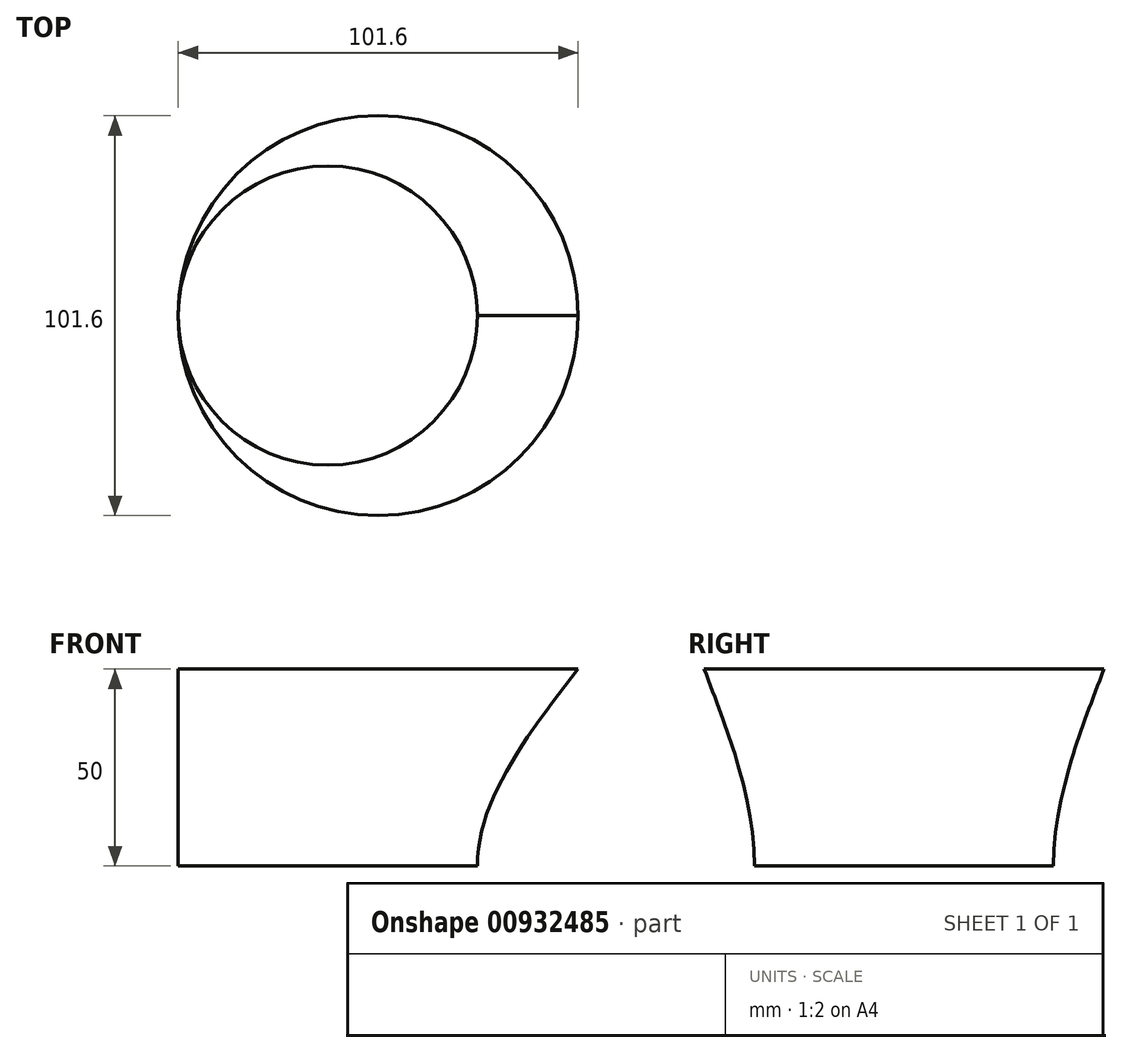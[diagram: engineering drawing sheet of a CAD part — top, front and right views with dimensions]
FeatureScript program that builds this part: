
annotation { "Feature Type Name" : "Feature", "Feature Type Description" : "" }
export const myFeature = defineFeature(function(context is Context, id is Id, definition is map)
    precondition{}
    {
        {
            var Q0;
            Q0=qCreatedBy(makeId("Top.planeOp"),FACE);
            var sketch = newSketch(context, id + "F0", { "sketchPlane" : qUnion([Q0])});
            skCircle(sketch, "E0", {"center": v(0, 0) * mm, "radius": 50.8 * mm});
            skSolve(sketch);
        }
        {
            var Q0;
            Q0=qCreatedBy(makeId("Top.planeOp"),FACE);
            cPlane(context, id + "F1", {"entities" : qUnion([Q0]), "cplaneType" : CPlaneType.OFFSET, "offset" : 50 * mm, "oppositeDirection" : true, "width" : 150 * mm, "height" : 150 * mm});
        }
        {
            var Q0;
            Q0=qCreatedBy(id+"F1.planeOp",FACE);
            var sketch = newSketch(context, id + "F2", { "sketchPlane" : qUnion([Q0])});
            skCircle(sketch, "E1.0", {"center": v(0, 0) * mm, "radius": 50.8 * mm});
            skCircle(sketch, "E2", {"center": v(-12.8, 0) * mm, "radius": 38 * mm});
            skPoint(sketch, "E2.first.point", {"position": v(-50.8, 0) * mm});
            skPoint(sketch, "E2.second.point", {"position": v(25.2, 0) * mm});
            skPoint(sketch, "E2.third.point", {"position": v(25.2, 0) * mm});
            skSolve(sketch);
        }
        {
            var Q0;
            Q0=makeQuery(id+"F0.imprint","IMPRINT",FACE,{"disambiguationData":[TD([[makeQuery(id+"F0.imprint","IMPRINT",EDGE,{"derivedFrom":sQuery(id+"F0.wireOp",EDGE,"E0")}),1.0]])]});
            var Q1;
            Q1=makeQuery(id+"F2.imprint","IMPRINT",FACE,{"disambiguationData":[TD([[makeQuery(id+"F2.imprint","IMPRINT",EDGE,{"derivedFrom":sQuery(id+"F2.wireOp",EDGE,"E2")}),1.0]])]});
            var Q2;
            Q2=sQuery(id+"F2.wireOp",EDGE,"E2");
            var Q3;
            Q3=sQuery(id+"F0.wireOp",EDGE,"E0");
            var Q4;
            Q4=sQuery(id+"F2.wireOp",EDGE,"E2");
            var Q5;
            Q5=sQuery(id+"F0.wireOp",EDGE,"E0");
            loft(context, id + "F3", {"bodyType" : ToolBodyType.SURFACE, "startCondition" : LoftEndDerivativeType.NORMAL_TO_PROFILE, "startMagnitude" : 1, "sheetProfilesArray" : [{ "sheetProfileEntities" : qUnion([Q0]) }, { "sheetProfileEntities" : qUnion([Q1]) }], "wireProfilesArray" : [{ "wireProfileEntities" : qUnion([Q2]) }, { "wireProfileEntities" : qUnion([Q3]) }], "guidesArray" : [{ "guideEntities" : qUnion([Q4]), "guideDerivativeType" : LoftGuideDerivativeType.DEFAULT, "guideDerivativeMagnitude" : 1 }, { "guideEntities" : qUnion([Q5]), "guideDerivativeType" : LoftGuideDerivativeType.DEFAULT, "guideDerivativeMagnitude" : 1 }]});
        }
    });
